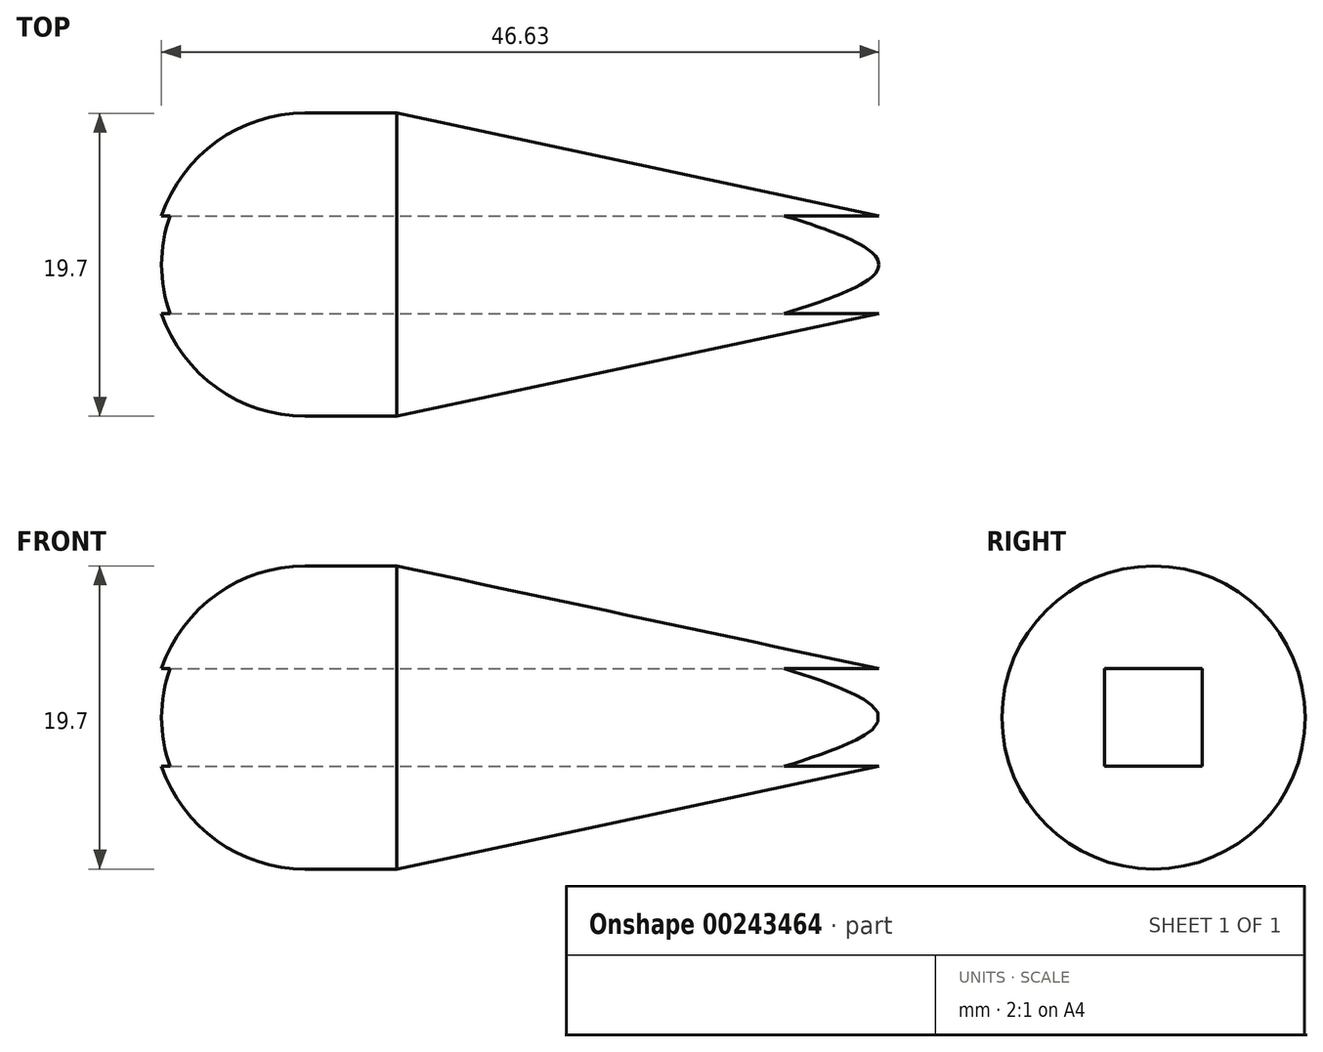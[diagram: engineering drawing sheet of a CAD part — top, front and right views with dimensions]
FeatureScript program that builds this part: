
annotation { "Feature Type Name" : "Feature", "Feature Type Description" : "" }
export const myFeature = defineFeature(function(context is Context, id is Id, definition is map)
    precondition{}
    {
        {
            var Q0;
            Q0=qCreatedBy(makeId("Top.planeOp"),FACE);
            var sketch = newSketch(context, id + "F0", { "sketchPlane" : qUnion([Q0])});
            skLineSegment(sketch, "E0", {"start": v(-46.6, 9.85) * mm, "end": v(-9.33, 1.92) * mm});
            skLineSegment(sketch, "E1", {"start": v(-7.76, -0.03) * mm, "end": v(-7.76, -0.03) * mm});
            skPoint(sketch, "E2.visualSharp", {"position": v(-7.76, 1.58) * mm});
            skArc(sketch, "E2.filletArc", {"start": v(-7.76, -0.03) * mm, "mid": v(-8.2, 1.22) * mm, "end": v(-9.33, 1.92) * mm});
            skLineSegment(sketch, "E3", {"start": v(-46.6, 9.85) * mm, "end": v(-52.55, 9.85) * mm});
            skLineSegment(sketch, "E4", {"start": v(-52.55, 9.85) * mm, "end": v(-52.55, 9.85) * mm});
            skArc(sketch, "E5", {"start": v(-52.55, 9.85) * mm, "mid": v(-59.52, 6.97) * mm, "end": v(-62.4, 0) * mm});
            skLineSegment(sketch, "E6", {"start": v(-71.36, 0) * mm, "end": v(0, 0) * mm});
            skSolve(sketch);
        }
        {
            var Q0;
            Q0=qCreatedBy(makeId("Right.planeOp"),FACE);
            var sketch = newSketch(context, id + "F1", { "sketchPlane" : qUnion([Q0])});
            skLineSegment(sketch, "E7.bottom", {"start": v(-3.17, -3.18) * mm, "end": v(3.18, -3.18) * mm});
            skLineSegment(sketch, "E7.top", {"start": v(-3.18, 3.18) * mm, "end": v(3.17, 3.18) * mm});
            skLineSegment(sketch, "E7.left", {"start": v(-3.17, -3.18) * mm, "end": v(-3.18, 3.18) * mm});
            skLineSegment(sketch, "E7.right", {"start": v(3.18, -3.18) * mm, "end": v(3.17, 3.18) * mm});
            skPoint(sketch, "E7.middle", {"position": v(0, 0) * mm});
            skSolve(sketch);
        }
        {
            var Q0;
            {var subQ2=sQuery(id+"F0.wireOp",EDGE,"E0");Q0=makeQuery(id+"F0.imprint","IMPRINT",FACE,{"disambiguationData":[TD([[makeQuery(id+"F0.imprint","IMPRINT",EDGE,{"derivedFrom":subQ2}),-1.0]])]});}
            var Q1;
            Q1=sQuery(id+"F0.wireOp",EDGE,"E6");
            revolve(context, id + "F2", {"entities" : qUnion([Q0]), "axis" : qUnion([Q1]), "revolveType" : RevolveType.FULL});
        }
        {
            var Q0;
            Q0=makeQuery(id+"F1.imprint","IMPRINT",FACE,{"disambiguationData":[TD([[makeQuery(id+"F1.imprint","IMPRINT",EDGE,{"derivedFrom":sQuery(id+"F1.wireOp",EDGE,"E7.bottom")}),1.0]])]});
            extrude(context, id + "F3", {"entities" : qUnion([Q0]), "operationType" : NewBodyOperationType.REMOVE, "endBound" : BoundingType.THROUGH_ALL, "oppositeDirection" : true, "depth" : 254 * mm});
        }
    });
